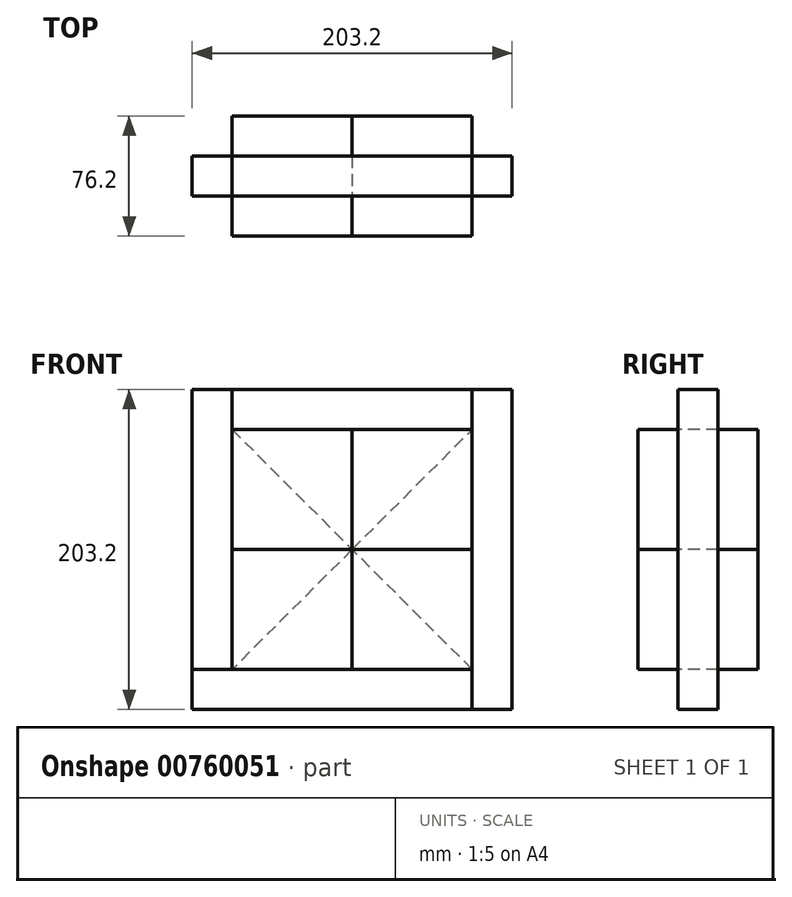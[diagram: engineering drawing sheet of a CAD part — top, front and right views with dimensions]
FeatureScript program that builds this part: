
annotation { "Feature Type Name" : "Feature", "Feature Type Description" : "" }
export const myFeature = defineFeature(function(context is Context, id is Id, definition is map)
    precondition{}
    {
        {
            var Q0;
            Q0=qCreatedBy(makeId("Front.planeOp"),FACE);
            var sketch = newSketch(context, id + "F0", { "sketchPlane" : qUnion([Q0])});
            skLineSegment(sketch, "E0.bottom", {"start": v(0, 0) * mm, "end": v(-76.2, 0) * mm});
            skLineSegment(sketch, "E0.top", {"start": v(0, 76.2) * mm, "end": v(-76.2, 76.2) * mm});
            skLineSegment(sketch, "E0.left", {"start": v(0, 0) * mm, "end": v(0, 76.2) * mm});
            skLineSegment(sketch, "E0.right", {"start": v(-76.2, 0) * mm, "end": v(-76.2, 76.2) * mm});
            skLineSegment(sketch, "E1.bottom", {"start": v(0, 0) * mm, "end": v(76.2, 0) * mm});
            skLineSegment(sketch, "E1.top", {"start": v(0, -76.2) * mm, "end": v(76.2, -76.2) * mm});
            skLineSegment(sketch, "E1.left", {"start": v(0, 0) * mm, "end": v(0, -76.2) * mm});
            skLineSegment(sketch, "E1.right", {"start": v(76.2, 0) * mm, "end": v(76.2, -76.2) * mm});
            skLineSegment(sketch, "E2.top", {"start": v(0, 76.2) * mm, "end": v(76.2, 76.2) * mm});
            skLineSegment(sketch, "E2.right", {"start": v(76.2, 0) * mm, "end": v(76.2, 76.2) * mm});
            skLineSegment(sketch, "E3.top", {"start": v(0, -76.2) * mm, "end": v(-76.2, -76.2) * mm});
            skLineSegment(sketch, "E3.right", {"start": v(-76.2, 0) * mm, "end": v(-76.2, -76.2) * mm});
            skSolve(sketch);
        }
        {
            var Q0;
            Q0=makeQuery(id+"F0.imprint","IMPRINT",FACE,{"disambiguationData":[TD([[makeQuery(id+"F0.imprint","IMPRINT",EDGE,{"derivedFrom":sQuery(id+"F0.wireOp",EDGE,"E0.top")}),1.0]])]});
            extrude(context, id + "F1", {"entities" : qUnion([Q0]), "depth" : 25.4 * mm, "offsetDistance" : 25.4 * mm});
        }
        {
            var Q0;
            Q0=makeQuery(id+"F0.imprint","IMPRINT",FACE,{"disambiguationData":[TD([[makeQuery(id+"F0.imprint","IMPRINT",EDGE,{"derivedFrom":sQuery(id+"F0.wireOp",EDGE,"E1.bottom")}),1.0]])]});
            extrude(context, id + "F2", {"entities" : qUnion([Q0]), "operationType" : NewBodyOperationType.ADD, "oppositeDirection" : true, "depth" : 25.4 * mm, "offsetDistance" : 25.4 * mm});
        }
        {
            var Q0;
            Q0=makeQuery(id+"F0.imprint","IMPRINT",FACE,{"disambiguationData":[TD([[makeQuery(id+"F0.imprint","IMPRINT",EDGE,{"derivedFrom":sQuery(id+"F0.wireOp",EDGE,"E1.top")}),1.0]])]});
            extrude(context, id + "F3", {"entities" : qUnion([Q0]), "depth" : 25.4 * mm, "offsetDistance" : 25.4 * mm});
        }
        {
            var Q0;
            Q0=makeQuery(id+"F0.imprint","IMPRINT",FACE,{"disambiguationData":[TD([[makeQuery(id+"F0.imprint","IMPRINT",EDGE,{"derivedFrom":sQuery(id+"F0.wireOp",EDGE,"E0.bottom")}),1.0]])]});
            extrude(context, id + "F4", {"entities" : qUnion([Q0]), "oppositeDirection" : true, "depth" : 25.4 * mm, "offsetDistance" : 25.4 * mm});
        }
        {
            var Q0;
            Q0=makeQuery(id+"F2.opExtrude","SWEPT_FACE",FACE,{"disambiguationData":[OSD([sQuery(id+"F0.wireOp",EDGE,"E2.top")])]});
            var sketch = newSketch(context, id + "F5", { "sketchPlane" : qUnion([Q0])});
            skLineSegment(sketch, "E4.bottom", {"start": v(76.2, 0) * mm, "end": v(-76.2, 0) * mm});
            skLineSegment(sketch, "E4.top", {"start": v(76.2, 25.4) * mm, "end": v(-76.2, 25.4) * mm});
            skLineSegment(sketch, "E4.left", {"start": v(76.2, 0) * mm, "end": v(76.2, 25.4) * mm});
            skLineSegment(sketch, "E4.right", {"start": v(-76.2, 0) * mm, "end": v(-76.2, 25.4) * mm});
            skSolve(sketch);
        }
        {
            var Q0;
            Q0 = qSketchRegion(id + "F5", true);
            extrude(context, id + "F6", {"entities" : qUnion([Q0]), "depth" : 25.4 * mm, "offsetDistance" : 25.4 * mm});
        }
        {
            var Q0;
            Q0=makeQuery(id+"F6.opExtrude","SWEPT_FACE",FACE,{"disambiguationData":[OSD([sQuery(id+"F5.wireOp",EDGE,"E4.right")])]});
            var sketch = newSketch(context, id + "F7", { "sketchPlane" : qUnion([Q0])});
            skLineSegment(sketch, "E5.bottom", {"start": v(-25.4, 101.6) * mm, "end": v(0, 101.6) * mm});
            skLineSegment(sketch, "E5.top", {"start": v(-25.4, -76.2) * mm, "end": v(0, -76.2) * mm});
            skLineSegment(sketch, "E5.left", {"start": v(-25.4, 101.6) * mm, "end": v(-25.4, -76.2) * mm});
            skLineSegment(sketch, "E5.right", {"start": v(0, 101.6) * mm, "end": v(0, -76.2) * mm});
            skSolve(sketch);
        }
        {
            var Q0;
            Q0 = qSketchRegion(id + "F7", true);
            extrude(context, id + "F8", {"entities" : qUnion([Q0]), "depth" : 25.4 * mm, "offsetDistance" : 25.4 * mm});
        }
        {
            var Q0;
            Q0=makeQuery(id+"F8.opExtrude","SWEPT_FACE",FACE,{"disambiguationData":[OSD([sQuery(id+"F7.wireOp",EDGE,"E5.top")])]});
            var sketch = newSketch(context, id + "F9", { "sketchPlane" : qUnion([Q0])});
            skLineSegment(sketch, "E6.bottom", {"start": v(-101.6, 0) * mm, "end": v(76.2, 0) * mm});
            skLineSegment(sketch, "E6.top", {"start": v(-101.6, -25.4) * mm, "end": v(76.2, -25.4) * mm});
            skLineSegment(sketch, "E6.left", {"start": v(-101.6, 0) * mm, "end": v(-101.6, -25.4) * mm});
            skLineSegment(sketch, "E6.right", {"start": v(76.2, 0) * mm, "end": v(76.2, -25.4) * mm});
            skSolve(sketch);
        }
        {
            var Q0;
            {var subQ2=sQuery(id+"F9.wireOp",EDGE,"E6.right");Q0=makeQuery(id+"F9.imprint","IMPRINT",FACE,{"disambiguationData":[TD([[makeQuery(id+"F9.imprint","IMPRINT",EDGE,{"derivedFrom":subQ2}),-1.0]])]});}
            var Q1;
            {var subQ2=sQuery(id+"F9.wireOp",EDGE,"E6.left");Q1=makeQuery(id+"F9.imprint","IMPRINT",FACE,{"disambiguationData":[TD([[makeQuery(id+"F9.imprint","IMPRINT",EDGE,{"derivedFrom":subQ2}),-1.0]])]});}
            extrude(context, id + "F10", {"entities" : qUnion([Q0, Q1]), "depth" : 25.4 * mm, "offsetDistance" : 25.4 * mm});
        }
        {
            var Q0;
            Q0=makeQuery(id+"F6.opExtrude","SWEPT_FACE",FACE,{"disambiguationData":[OSD([sQuery(id+"F5.wireOp",EDGE,"E4.left")])]});
            var sketch = newSketch(context, id + "F11", { "sketchPlane" : qUnion([Q0])});
            skLineSegment(sketch, "E7.bottom", {"start": v(0, 101.6) * mm, "end": v(25.4, 101.6) * mm});
            skLineSegment(sketch, "E7.top", {"start": v(0, -101.6) * mm, "end": v(25.4, -101.6) * mm});
            skLineSegment(sketch, "E7.left", {"start": v(0, 101.6) * mm, "end": v(0, -101.6) * mm});
            skLineSegment(sketch, "E7.right", {"start": v(25.4, 101.6) * mm, "end": v(25.4, -101.6) * mm});
            skSolve(sketch);
        }
        {
            var Q0;
            Q0 = qSketchRegion(id + "F11", true);
            extrude(context, id + "F12", {"entities" : qUnion([Q0]), "depth" : 25.4 * mm, "offsetDistance" : 25.4 * mm});
        }
        {
            var Q0;
            Q0=makeQuery(id+"F3.opExtrude","CAP_FACE",FACE,{"disambiguationData":[OSD([sQuery(id+"F0.wireOp",EDGE,"E1.top"),sQuery(id+"F0.wireOp",EDGE,"E1.right"),sQuery(id+"F0.wireOp",EDGE,"E1.bottom"),sQuery(id+"F0.wireOp",EDGE,"E1.left")])],"isStart":true});
            var sketch = newSketch(context, id + "F13", { "sketchPlane" : qUnion([Q0])});
            skLineSegment(sketch, "E8", {"start": v(-76.2, -76.2) * mm, "end": v(0, 0) * mm});
            skLineSegment(sketch, "E9", {"start": v(0, 0) * mm, "end": v(0, -76.2) * mm});
            skLineSegment(sketch, "E10", {"start": v(0, -76.2) * mm, "end": v(-76.2, -76.2) * mm});
            skSolve(sketch);
        }
        {
            var Q0;
            Q0=makeQuery(id+"F13.imprint","IMPRINT",FACE,{"disambiguationData":[TD([[makeQuery(id+"F13.imprint","IMPRINT",EDGE,{"derivedFrom":sQuery(id+"F13.wireOp",EDGE,"E8")}),-1.0]])]});
            extrude(context, id + "F14", {"entities" : qUnion([Q0]), "depth" : 50.8 * mm, "offsetDistance" : 25.4 * mm});
        }
        {
            var Q0;
            Q0=makeQuery(id+"F1.opExtrude","CAP_FACE",FACE,{"disambiguationData":[OSD([sQuery(id+"F0.wireOp",EDGE,"E0.top"),sQuery(id+"F0.wireOp",EDGE,"E0.right"),sQuery(id+"F0.wireOp",EDGE,"E0.left"),sQuery(id+"F0.wireOp",EDGE,"E0.bottom")])],"isStart":true});
            var sketch = newSketch(context, id + "F15", { "sketchPlane" : qUnion([Q0])});
            skLineSegment(sketch, "E11", {"start": v(76.2, 76.2) * mm, "end": v(0, 0) * mm});
            skSolve(sketch);
        }
        {
            var Q0;
            Q0=makeQuery(id+"F15.imprint","IMPRINT",FACE,{"disambiguationData":[TD([[makeQuery(id+"F15.imprint","IMPRINT",EDGE,{"derivedFrom":sQuery(id+"F15.wireOp",EDGE,"E11")}),-1.0]])]});
            extrude(context, id + "F16", {"entities" : qUnion([Q0]), "depth" : 50.8 * mm, "offsetDistance" : 25.4 * mm});
        }
        {
            var Q0;
            Q0=makeQuery(id+"F2.opExtrude","CAP_FACE",FACE,{"disambiguationData":[OSD([sQuery(id+"F0.wireOp",EDGE,"E1.bottom"),sQuery(id+"F0.wireOp",EDGE,"E2.top"),sQuery(id+"F0.wireOp",EDGE,"E0.left"),sQuery(id+"F0.wireOp",EDGE,"E2.right")])],"isStart":false});
            var sketch = newSketch(context, id + "F17", { "sketchPlane" : qUnion([Q0])});
            skLineSegment(sketch, "E12", {"start": v(0, 0) * mm, "end": v(-76.2, 76.2) * mm});
            skSolve(sketch);
        }
        {
            var Q0;
            Q0=makeQuery(id+"F17.imprint","IMPRINT",FACE,{"disambiguationData":[TD([[makeQuery(id+"F17.imprint","IMPRINT",EDGE,{"derivedFrom":sQuery(id+"F17.wireOp",EDGE,"E12")}),1.0]])]});
            extrude(context, id + "F18", {"entities" : qUnion([Q0]), "depth" : 25.4 * mm, "offsetDistance" : 25.4 * mm});
        }
        {
            var Q0;
            Q0=makeQuery(id+"F4.opExtrude","CAP_FACE",FACE,{"disambiguationData":[OSD([sQuery(id+"F0.wireOp",EDGE,"E0.bottom"),sQuery(id+"F0.wireOp",EDGE,"E3.top"),sQuery(id+"F0.wireOp",EDGE,"E1.left"),sQuery(id+"F0.wireOp",EDGE,"E3.right")])],"isStart":false});
            var sketch = newSketch(context, id + "F19", { "sketchPlane" : qUnion([Q0])});
            skLineSegment(sketch, "E13", {"start": v(0, 0) * mm, "end": v(76.2, -76.2) * mm});
            skSolve(sketch);
        }
        {
            var Q0;
            Q0=makeQuery(id+"F19.imprint","IMPRINT",FACE,{"disambiguationData":[TD([[makeQuery(id+"F19.imprint","IMPRINT",EDGE,{"derivedFrom":sQuery(id+"F19.wireOp",EDGE,"E13")}),1.0]])]});
            extrude(context, id + "F20", {"entities" : qUnion([Q0]), "depth" : 25.4 * mm, "offsetDistance" : 25.4 * mm});
        }
    });
